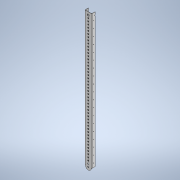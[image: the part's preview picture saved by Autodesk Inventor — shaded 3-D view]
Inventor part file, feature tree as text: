
AUTODESK INVENTOR PART (.ipt)
format: ipt  version: 2022 (Build 260153000, 153)  size: 673,280 bytes
history: native  units: mm
features: sketch x6, extrude x5, sheet_metal_op x3, projected_geometry x3, other x2, pattern_linear x1
ambient origin geometry x8: Origin, YZ Plane, XZ Plane, XY Plane, X Axis, Y Axis, Z Axis, Center Point
bodies: Solid1 (feature_tree)
feature tree (20):
  sheet_metal_op  "Contour Flange1"
  extrude  "Extrusion1"  Depth=50.0mm
  extrude  "Extrusion2"  Depth=1.5mm
  extrude  "Extrusion4"  Depth=1.5mm
  pattern_linear  "Rectangular Pattern1"  Count1=100  [1 undecoded]
  extrude  "Extrusion5"  Depth=1.5mm
  extrude  "Extrusion6"  Depth=10.0mm
  sketch  "Sketch1"  dims[d3=25.0mm d4=50.0mm]
  other  "Plate1"
  sheet_metal_op  "Bend1"
  sheet_metal_op  "Corner1"
  sketch  "Sketch2"  dims[d5=25.0mm d6=1.5mm]
  sketch  "Sketch3"  dims[d7=1.5mm d8=0.75mm]
  projected_geometry  "Projected Loop1"
  projected_geometry  "Projected Loop2"
  sketch  "Sketch5"  dims[d9=3.0mm]
  sketch  "Sketch6"  dims[d10=1.5mm d11=1000.0mm]
  projected_geometry  "Projected Loop5"
  sketch  "Sketch7"  dims[d12=1.5mm d13=1.5mm d14=6.0mm d15=1.5mm d16=1.5mm d17=20.0mm d18=10.0mm d19=25.0mm d20=490.0mm d22=20.0mm d23=10.0mm d25=10.0mm d27=0.0mm d28=0.0mm d29=0.0mm d30=0.0mm d33=3.35mm d34=11.0mm d35=28.0mm d36=0.0mm d37=0.0mm d38=190.0mm d40=50.0mm d41=15.0mm d42=10.0mm d43=0.0mm d44=8.0mm d45=20.0mm d46=0.0mm d47=0.0mm]
  other  "Definition1"
note: 1 required parameter value undecoded (feature->parameter linkage not recoverable at this tier; creation-order binding heuristic only, values carry confidence <= 0.55)
